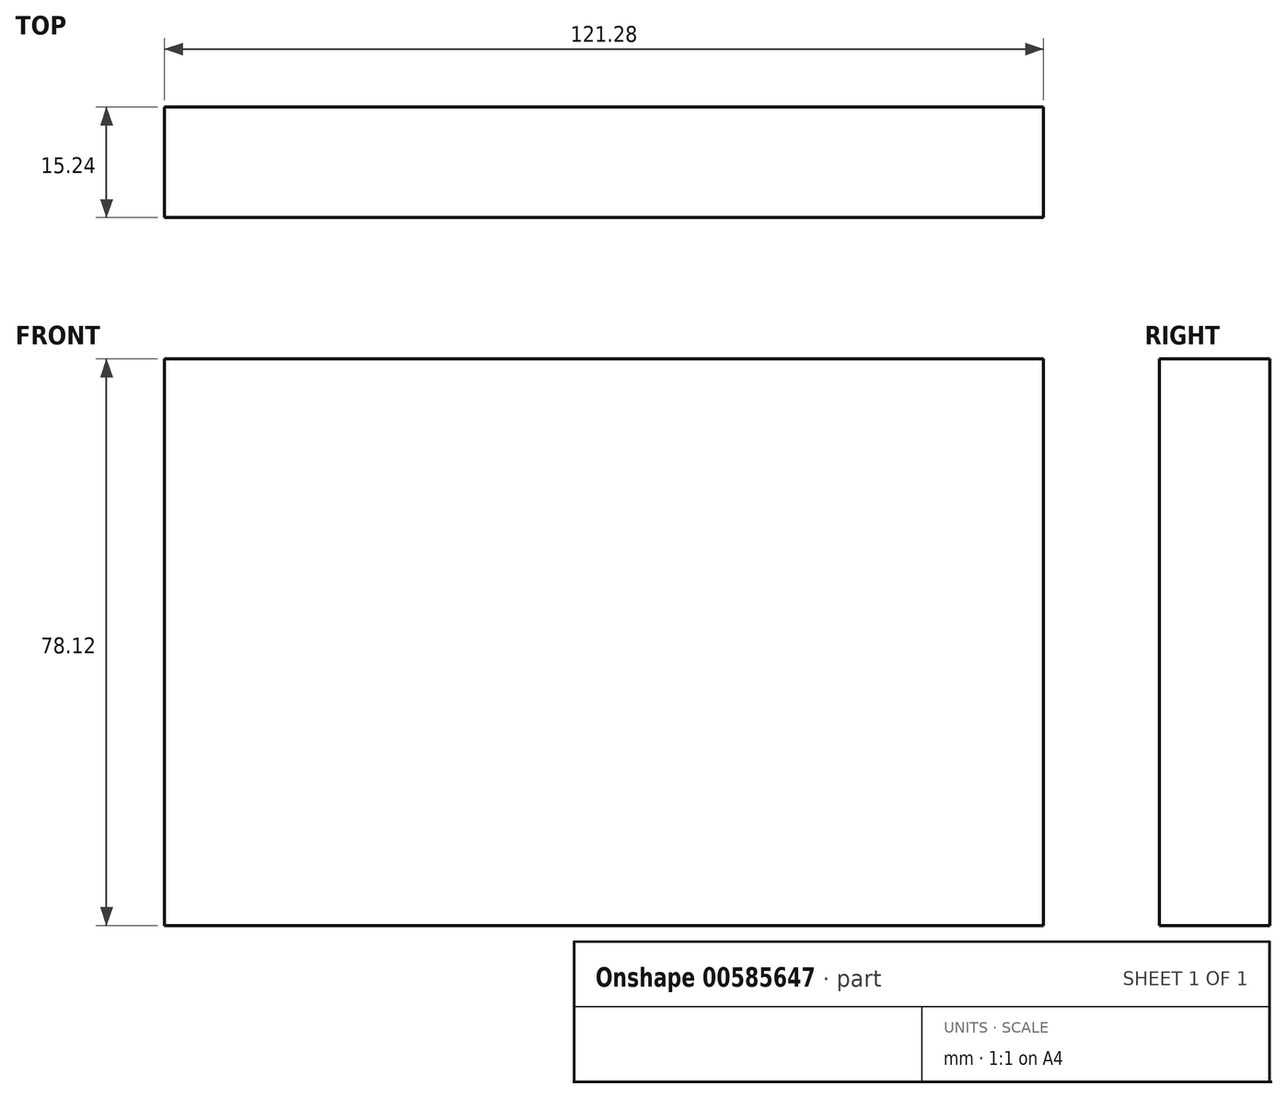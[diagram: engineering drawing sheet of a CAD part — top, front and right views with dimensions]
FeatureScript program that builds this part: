
annotation { "Feature Type Name" : "Feature", "Feature Type Description" : "" }
export const myFeature = defineFeature(function(context is Context, id is Id, definition is map)
    precondition{}
    {
        {
            var Q0;
            Q0=qCreatedBy(makeId("Front.planeOp"),FACE);
            var sketch = newSketch(context, id + "F0", { "sketchPlane" : qUnion([Q0])});
            skLineSegment(sketch, "E0.bottom", {"start": v(-60.64, 39.06) * mm, "end": v(60.64, 39.06) * mm});
            skLineSegment(sketch, "E0.top", {"start": v(-60.64, -39.06) * mm, "end": v(60.64, -39.06) * mm});
            skLineSegment(sketch, "E0.left", {"start": v(-60.64, 39.06) * mm, "end": v(-60.64, -39.06) * mm});
            skLineSegment(sketch, "E0.right", {"start": v(60.64, 39.06) * mm, "end": v(60.64, -39.06) * mm});
            skPoint(sketch, "E0.middle", {"position": v(0, 0) * mm});
            skSolve(sketch);
        }
        {
            var Q0;
            Q0=makeQuery(id+"F0.imprint","IMPRINT",FACE,{"disambiguationData":[TD([[makeQuery(id+"F0.imprint","IMPRINT",EDGE,{"derivedFrom":sQuery(id+"F0.wireOp",EDGE,"E0.bottom")}),-1.0]])]});
            extrude(context, id + "F1", {"entities" : qUnion([Q0]), "depth" : 15.24 * mm, "offsetDistance" : 25.4 * mm});
        }
    });
